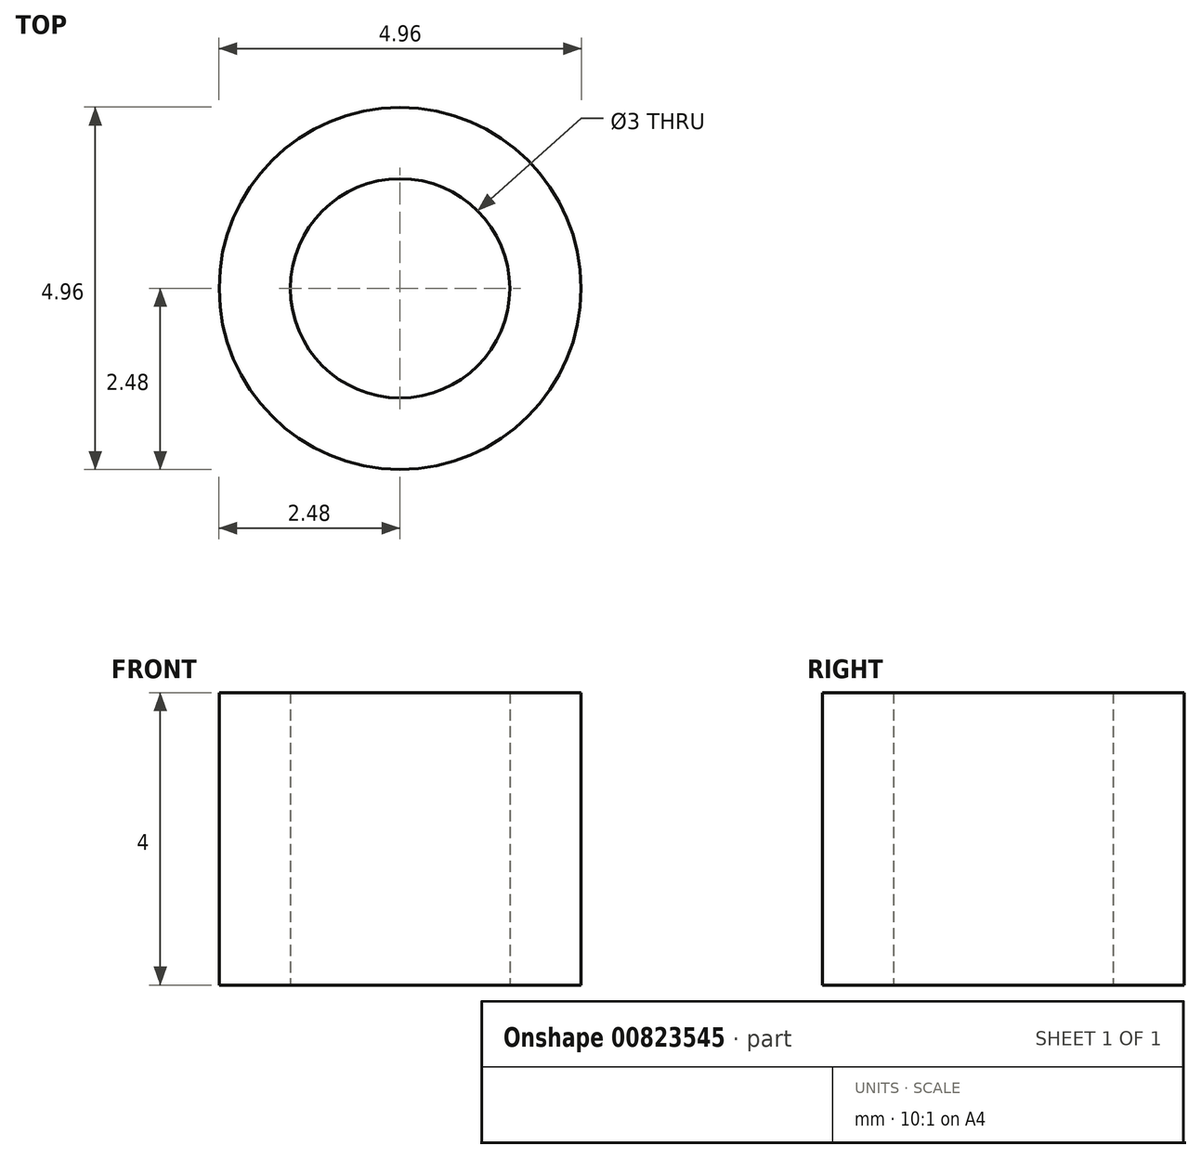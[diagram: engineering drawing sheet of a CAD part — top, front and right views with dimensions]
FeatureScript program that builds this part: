
annotation { "Feature Type Name" : "Feature", "Feature Type Description" : "" }
export const myFeature = defineFeature(function(context is Context, id is Id, definition is map)
    precondition{}
    {
        {
            var Q0;
            Q0=qCreatedBy(makeId("Top.planeOp"),FACE);
            var sketch = newSketch(context, id + "F0", { "sketchPlane" : qUnion([Q0])});
            skCircle(sketch, "E0", {"center": v(0, 0) * mm, "radius": 1.5 * mm});
            skCircle(sketch, "E1", {"center": v(0, 0) * mm, "radius": 2.48 * mm});
            skSolve(sketch);
        }
        {
            var Q0;
            Q0=makeQuery(id+"F0.imprint","IMPRINT",FACE,{"disambiguationData":[TD([[makeQuery(id+"F0.imprint","IMPRINT",EDGE,{"derivedFrom":sQuery(id+"F0.wireOp",EDGE,"E0")}),-1.0]])]});
            extrude(context, id + "F1", {"entities" : qUnion([Q0]), "depth" : 4 * mm, "offsetDistance" : 25 * mm});
        }
    });
